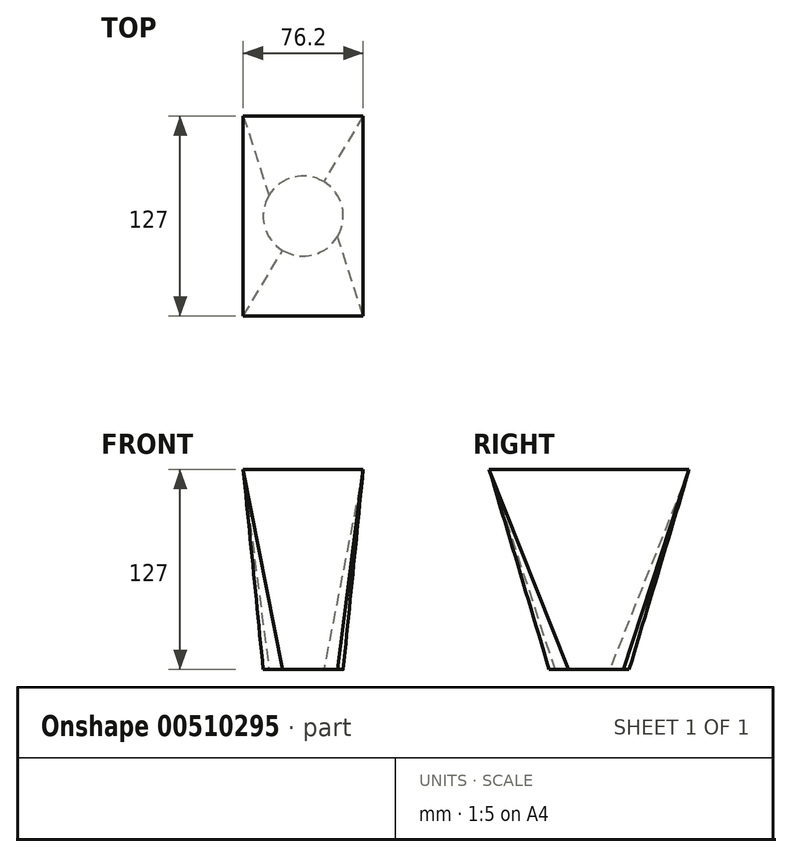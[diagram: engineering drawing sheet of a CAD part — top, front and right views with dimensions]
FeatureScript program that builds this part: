
annotation { "Feature Type Name" : "Feature", "Feature Type Description" : "" }
export const myFeature = defineFeature(function(context is Context, id is Id, definition is map)
    precondition{}
    {
        {
            var Q0;
            Q0=qCreatedBy(makeId("Top.planeOp"),FACE);
            var sketch = newSketch(context, id + "F0", { "sketchPlane" : qUnion([Q0])});
            skCircle(sketch, "E0", {"center": v(0, 0) * mm, "radius": 25.4 * mm});
            skSolve(sketch);
        }
        {
            var Q0;
            Q0=qCreatedBy(makeId("Top.planeOp"),FACE);
            cPlane(context, id + "F1", {"entities" : qUnion([Q0]), "cplaneType" : CPlaneType.OFFSET, "offset" : 127 * mm, "width" : 152.4 * mm, "height" : 152.4 * mm});
        }
        {
            var Q0;
            Q0=qCreatedBy(id+"F1.planeOp",FACE);
            var sketch = newSketch(context, id + "F2", { "sketchPlane" : qUnion([Q0])});
            skLineSegment(sketch, "E1.bottom", {"start": v(-38.1, -63.5) * mm, "end": v(38.1, -63.5) * mm});
            skLineSegment(sketch, "E1.top", {"start": v(-38.1, 63.5) * mm, "end": v(38.1, 63.5) * mm});
            skLineSegment(sketch, "E1.left", {"start": v(-38.1, -63.5) * mm, "end": v(-38.1, 63.5) * mm});
            skLineSegment(sketch, "E1.right", {"start": v(38.1, -63.5) * mm, "end": v(38.1, 63.5) * mm});
            skPoint(sketch, "E1.middle", {"position": v(0, 0) * mm});
            skSolve(sketch);
        }
        {
            var Q0;
            Q0=makeQuery(id+"F2.imprint","IMPRINT",FACE,{"disambiguationData":[TD([[makeQuery(id+"F2.imprint","IMPRINT",EDGE,{"derivedFrom":sQuery(id+"F2.wireOp",EDGE,"E1.bottom")}),1.0]])]});
            var Q1;
            Q1=makeQuery(id+"F0.imprint","IMPRINT",FACE,{"disambiguationData":[TD([[makeQuery(id+"F0.imprint","IMPRINT",EDGE,{"derivedFrom":sQuery(id+"F0.wireOp",EDGE,"E0")}),1.0]])]});
            loft(context, id + "F3", {"sheetProfilesArray" : [{ "sheetProfileEntities" : qUnion([Q0]) }, { "sheetProfileEntities" : qUnion([Q1]) }]});
        }
    });
